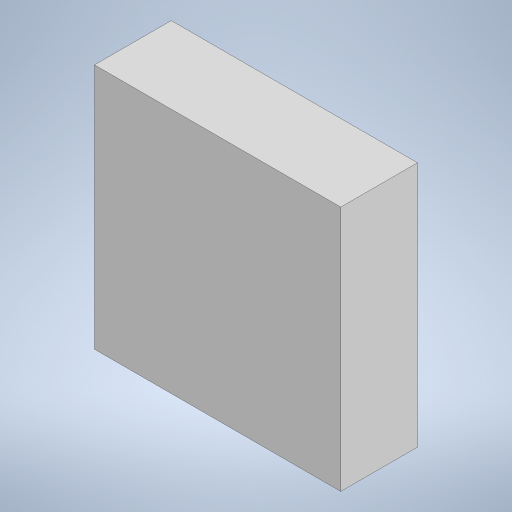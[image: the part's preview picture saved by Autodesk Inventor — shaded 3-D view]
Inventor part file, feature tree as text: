
AUTODESK INVENTOR PART (.ipt)
format: ipt  version: 2023 (Build 270158000, 158)  size: 195,072 bytes
history: native  units: in
note: dims shown in document units (in); Inventor stores cm internally (conversion verified against a paired STEP export)
features: extrude x2, sketch x2, projected_geometry x1
ambient origin geometry x8: Origin, YZ Plane, XZ Plane, XY Plane, X Axis, Y Axis, Z Axis, Center Point
bodies: Solid1 (feature_tree)
feature tree (5):
  extrude  "Extrusion1"  Depth=3.01in
  extrude  "Extrusion2"  Depth=1.0in
  sketch  "Sketch1"  dims[d0=3.01in d1=3.01in]
  sketch  "Sketch2"  dims[d2=1.505in d3=1.505in d4=0.1in d5=0.0in d6=0.1in d7=1.0in d8=0.0in]
  projected_geometry  "Projected Loop1"
